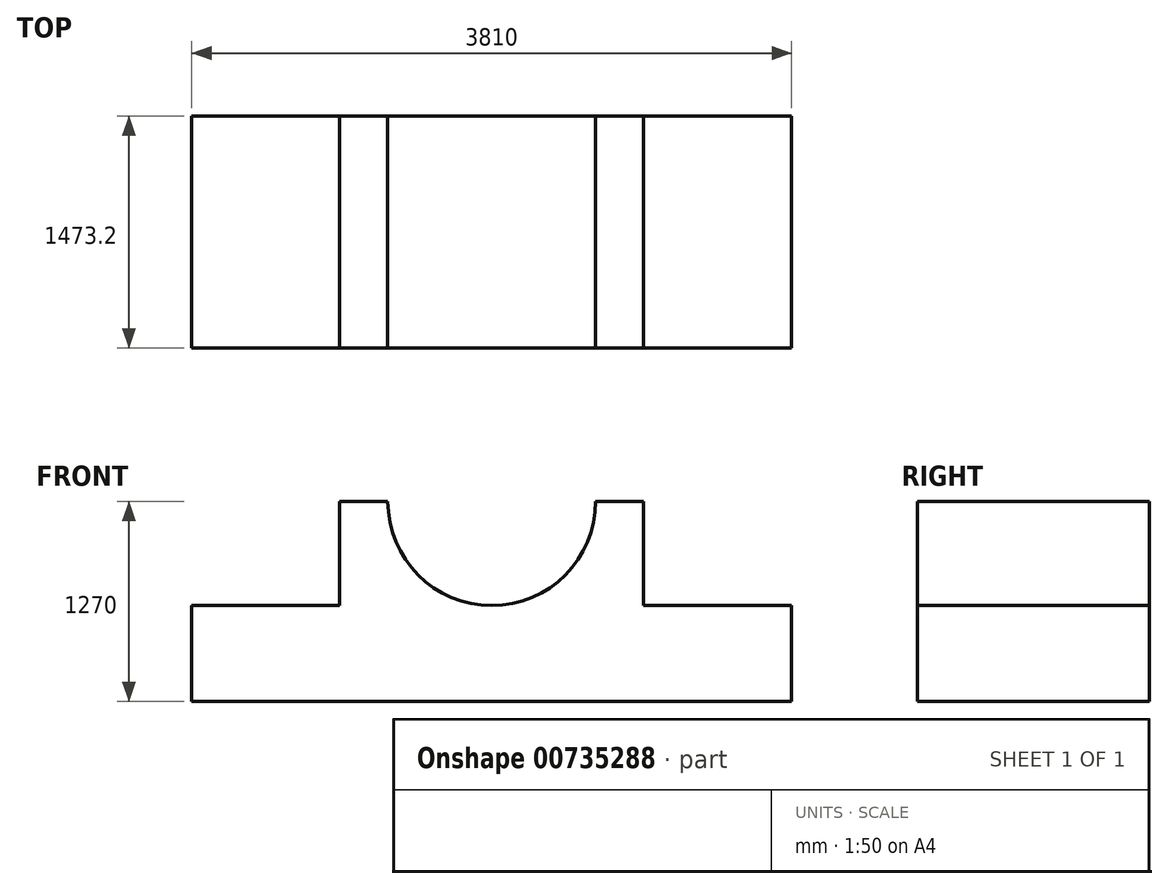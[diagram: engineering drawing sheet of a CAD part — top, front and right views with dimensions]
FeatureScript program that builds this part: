
annotation { "Feature Type Name" : "Feature", "Feature Type Description" : "" }
export const myFeature = defineFeature(function(context is Context, id is Id, definition is map)
    precondition{}
    {
        {
            var Q0;
            Q0=qCreatedBy(makeId("Front.planeOp"),FACE);
            var sketch = newSketch(context, id + "F0", { "sketchPlane" : qUnion([Q0])});
            skLineSegment(sketch, "E0.bottom", {"start": v(-1905, -609.6) * mm, "end": v(1905, -609.6) * mm});
            skPoint(sketch, "E0.middle", {"position": v(0, 0) * mm});
            skLineSegment(sketch, "E1", {"start": v(-1905, -609.6) * mm, "end": v(-1905, 0) * mm});
            skLineSegment(sketch, "E2", {"start": v(1905, -609.6) * mm, "end": v(1905, 0) * mm});
            skLineSegment(sketch, "E3", {"start": v(-1905, 0) * mm, "end": v(-965.2, 0) * mm});
            skLineSegment(sketch, "E4", {"start": v(1905, 0) * mm, "end": v(965.2, 0) * mm});
            skLineSegment(sketch, "E5", {"start": v(-965.2, 0) * mm, "end": v(-965.2, 660.4) * mm});
            skLineSegment(sketch, "E6", {"start": v(965.2, 0) * mm, "end": v(965.2, 660.4) * mm});
            skLineSegment(sketch, "E7", {"start": v(-965.2, 660.4) * mm, "end": v(-660.4, 660.4) * mm});
            skLineSegment(sketch, "E8", {"start": v(-660.4, 660.4) * mm, "end": v(0, 660.4) * mm});
            skCircle(sketch, "E9", {"center": v(0, 660.4) * mm, "radius": 660.4 * mm});
            skLineSegment(sketch, "E10", {"start": v(965.2, 660.4) * mm, "end": v(660.4, 660.4) * mm});
            skSolve(sketch);
        }
        {
            var Q0;
            Q0=makeQuery(id+"F0.imprint","IMPRINT",FACE,{"disambiguationData":[TD([[makeQuery(id+"F0.imprint","IMPRINT",EDGE,{"derivedFrom":sQuery(id+"F0.wireOp",EDGE,"E0.bottom")}),1.0]])]});
            var sketch = newSketch(context, id + "F1", { "sketchPlane" : qUnion([Q0])});
            skSolve(sketch);
        }
        {
            var Q0;
            Q0 = qSketchRegion(id + "F1", true);
            var Q1;
            Q1=makeQuery(id+"F0.imprint","IMPRINT",FACE,{"disambiguationData":[TD([[makeQuery(id+"F0.imprint","IMPRINT",EDGE,{"derivedFrom":sQuery(id+"F0.wireOp",EDGE,"E0.bottom")}),1.0]])]});
            extrude(context, id + "F2", {"entities" : qUnion([Q0, Q1]), "depth" : 1473.2 * mm, "offsetDistance" : 25.4 * mm});
        }
    });
